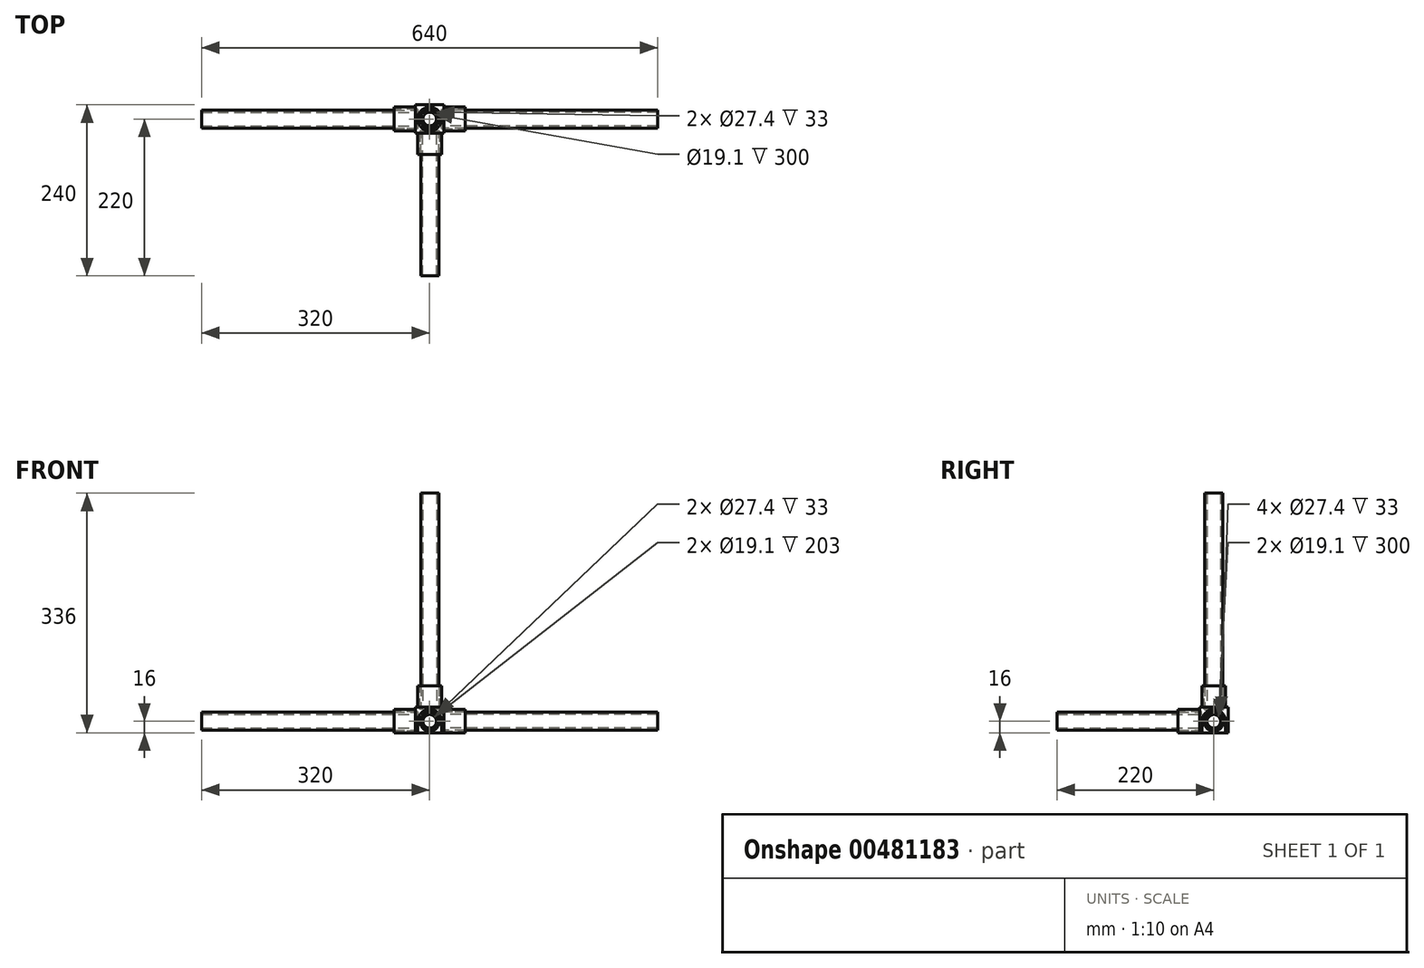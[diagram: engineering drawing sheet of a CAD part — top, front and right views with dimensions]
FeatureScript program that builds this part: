
annotation { "Feature Type Name" : "Feature", "Feature Type Description" : "" }
export const myFeature = defineFeature(function(context is Context, id is Id, definition is map)
    precondition{}
    {
        {
            var Q0;
            Q0=qCreatedBy(makeId("Front.planeOp"),FACE);
            var sketch = newSketch(context, id + "F0", { "sketchPlane" : qUnion([Q0])});
            skLineSegment(sketch, "E0.bottom", {"start": v(20, 20) * mm, "end": v(-20, 20) * mm});
            skLineSegment(sketch, "E0.top", {"start": v(20, -20) * mm, "end": v(-20, -20) * mm});
            skLineSegment(sketch, "E0.left", {"start": v(20, 20) * mm, "end": v(20, -20) * mm});
            skLineSegment(sketch, "E0.right", {"start": v(-20, 20) * mm, "end": v(-20, -20) * mm});
            skPoint(sketch, "E0.middle", {"position": v(0, 0) * mm});
            skSolve(sketch);
        }
        {
            var Q0;
            Q0=makeQuery(id+"F0.imprint","IMPRINT",FACE,{"disambiguationData":[TD([[makeQuery(id+"F0.imprint","IMPRINT",EDGE,{"derivedFrom":sQuery(id+"F0.wireOp",EDGE,"E0.bottom")}),1.0]])]});
            extrude(context, id + "F1", {"entities" : qUnion([Q0]), "endBound" : BoundingType.SYMMETRIC, "depth" : 40 * mm});
        }
        {
            var Q0;
            Q0=makeQuery(id+"F1.opExtrude","CAP_FACE",FACE,{"disambiguationData":[OSD([sQuery(id+"F0.wireOp",EDGE,"E0.bottom"),sQuery(id+"F0.wireOp",EDGE,"E0.top"),sQuery(id+"F0.wireOp",EDGE,"E0.left"),sQuery(id+"F0.wireOp",EDGE,"E0.right")])],"isStart":false});
            var sketch = newSketch(context, id + "F2", { "sketchPlane" : qUnion([Q0])});
            skLineSegment(sketch, "E1.bottom", {"start": v(20, 20) * mm, "end": v(-20, 20) * mm});
            skLineSegment(sketch, "E1.top", {"start": v(20, -20) * mm, "end": v(-20, -20) * mm});
            skLineSegment(sketch, "E1.left", {"start": v(20, 20) * mm, "end": v(20, -20) * mm});
            skLineSegment(sketch, "E1.right", {"start": v(-20, 20) * mm, "end": v(-20, -20) * mm});
            skPoint(sketch, "E1.middle", {"position": v(0, 0) * mm});
            skCircle(sketch, "E2", {"center": v(0, 0) * mm, "radius": 12.7 * mm});
            skCircle(sketch, "E3.0", {"center": v(0, 0) * mm, "radius": 9.55 * mm});
            skCircle(sketch, "E4.0", {"center": v(0, 0) * mm, "radius": 13.7 * mm});
            skCircle(sketch, "E5.0", {"center": v(0, 0) * mm, "radius": 16.7 * mm});
            skSolve(sketch);
        }
        {
            var Q0;
            Q0=makeQuery(id+"F2.imprint","IMPRINT",FACE,{"disambiguationData":[TD([[makeQuery(id+"F2.imprint","IMPRINT",EDGE,{"derivedFrom":sQuery(id+"F2.wireOp",EDGE,"E2")}),-1.0]])]});
            var Q1;
            Q1=makeQuery(id+"F2.imprint","IMPRINT",FACE,{"disambiguationData":[TD([[makeQuery(id+"F2.imprint","IMPRINT",EDGE,{"derivedFrom":sQuery(id+"F2.wireOp",EDGE,"E2")}),1.0]])]});
            var Q2;
            Q2=makeQuery(id+"F2.imprint","IMPRINT",FACE,{"disambiguationData":[TD([[makeQuery(id+"F2.imprint","IMPRINT",EDGE,{"derivedFrom":sQuery(id+"F2.wireOp",EDGE,"E3.0")}),1.0]])]});
            extrude(context, id + "F3", {"entities" : qUnion([Q0, Q1, Q2]), "operationType" : NewBodyOperationType.REMOVE, "oppositeDirection" : true, "depth" : 3 * mm});
        }
        {
            var Q0;
            Q0=makeQuery(id+"F2.imprint","IMPRINT",FACE,{"disambiguationData":[TD([[makeQuery(id+"F2.imprint","IMPRINT",EDGE,{"derivedFrom":sQuery(id+"F2.wireOp",EDGE,"E2")}),1.0]])]});
            extrude(context, id + "F4", {"entities" : qUnion([Q0]), "depth" : 200 * mm});
        }
        {
            var Q0;
            Q0=makeQuery(id+"F4.opExtrude","CAP_FACE",FACE,{"disambiguationData":[OSD([sQuery(id+"F2.wireOp",EDGE,"E2"),sQuery(id+"F2.wireOp",EDGE,"E3.0")])],"isStart":true});
            extrude(context, id + "F5", {"entities" : qUnion([Q0]), "operationType" : NewBodyOperationType.ADD, "depth" : 3 * mm});
        }
        {
            var Q0;
            Q0=makeQuery(id+"F2.imprint","IMPRINT",FACE,{"disambiguationData":[TD([[makeQuery(id+"F2.imprint","IMPRINT",EDGE,{"derivedFrom":sQuery(id+"F2.wireOp",EDGE,"E4.0")}),-1.0]])]});
            extrude(context, id + "F6", {"entities" : qUnion([Q0]), "operationType" : NewBodyOperationType.ADD, "depth" : 30 * mm});
        }
        {
            var Q0;
            Q0=makeQuery(id+"F1.opExtrude","SWEPT_FACE",FACE,{"disambiguationData":[OSD([sQuery(id+"F0.wireOp",EDGE,"E0.left")])]});
            var sketch = newSketch(context, id + "F7", { "sketchPlane" : qUnion([Q0])});
            skLineSegment(sketch, "E6.bottom", {"start": v(20, 20) * mm, "end": v(-20, 20) * mm});
            skLineSegment(sketch, "E6.top", {"start": v(20, -20) * mm, "end": v(-20, -20) * mm});
            skLineSegment(sketch, "E6.left", {"start": v(20, 20) * mm, "end": v(20, -20) * mm});
            skLineSegment(sketch, "E6.right", {"start": v(-20, 20) * mm, "end": v(-20, -20) * mm});
            skPoint(sketch, "E6.middle", {"position": v(0, 0) * mm});
            skCircle(sketch, "E7", {"center": v(0, 0) * mm, "radius": 12.7 * mm});
            skCircle(sketch, "E8.0", {"center": v(0, 0) * mm, "radius": 9.55 * mm});
            skCircle(sketch, "E9.0", {"center": v(0, 0) * mm, "radius": 13.7 * mm});
            skCircle(sketch, "E10.0", {"center": v(0, 0) * mm, "radius": 16.7 * mm});
            skSolve(sketch);
        }
        {
            var Q0;
            Q0=makeQuery(id+"F7.imprint","IMPRINT",FACE,{"disambiguationData":[TD([[makeQuery(id+"F7.imprint","IMPRINT",EDGE,{"derivedFrom":sQuery(id+"F7.wireOp",EDGE,"E7")}),-1.0]])]});
            var Q1;
            Q1=makeQuery(id+"F7.imprint","IMPRINT",FACE,{"disambiguationData":[TD([[makeQuery(id+"F7.imprint","IMPRINT",EDGE,{"derivedFrom":sQuery(id+"F7.wireOp",EDGE,"E7")}),1.0]])]});
            var Q2;
            Q2=makeQuery(id+"F7.imprint","IMPRINT",FACE,{"disambiguationData":[TD([[makeQuery(id+"F7.imprint","IMPRINT",EDGE,{"derivedFrom":sQuery(id+"F7.wireOp",EDGE,"E8.0")}),1.0]])]});
            extrude(context, id + "F8", {"entities" : qUnion([Q0, Q1, Q2]), "operationType" : NewBodyOperationType.REMOVE, "oppositeDirection" : true, "depth" : 3 * mm});
        }
        {
            var Q0;
            Q0=makeQuery(id+"F7.imprint","IMPRINT",FACE,{"disambiguationData":[TD([[makeQuery(id+"F7.imprint","IMPRINT",EDGE,{"derivedFrom":sQuery(id+"F7.wireOp",EDGE,"E7")}),1.0]])]});
            extrude(context, id + "F9", {"entities" : qUnion([Q0]), "depth" : 300 * mm});
        }
        {
            var Q0;
            Q0=makeQuery(id+"F7.imprint","IMPRINT",FACE,{"disambiguationData":[TD([[makeQuery(id+"F7.imprint","IMPRINT",EDGE,{"derivedFrom":sQuery(id+"F7.wireOp",EDGE,"E9.0")}),-1.0]])]});
            extrude(context, id + "F10", {"entities" : qUnion([Q0]), "operationType" : NewBodyOperationType.ADD, "depth" : 30 * mm});
        }
        {
            var Q0;
            Q0=makeQuery(id+"F1.opExtrude","SWEPT_FACE",FACE,{"disambiguationData":[OSD([sQuery(id+"F0.wireOp",EDGE,"E0.right")])]});
            var sketch = newSketch(context, id + "F11", { "sketchPlane" : qUnion([Q0])});
            skLineSegment(sketch, "E11.bottom", {"start": v(20, 20) * mm, "end": v(-20, 20) * mm});
            skLineSegment(sketch, "E11.top", {"start": v(20, -20) * mm, "end": v(-20, -20) * mm});
            skLineSegment(sketch, "E11.left", {"start": v(20, 20) * mm, "end": v(20, -20) * mm});
            skLineSegment(sketch, "E11.right", {"start": v(-20, 20) * mm, "end": v(-20, -20) * mm});
            skPoint(sketch, "E11.middle", {"position": v(0, 0) * mm});
            skCircle(sketch, "E12", {"center": v(0, 0) * mm, "radius": 12.7 * mm});
            skCircle(sketch, "E13.0", {"center": v(0, 0) * mm, "radius": 9.55 * mm});
            skCircle(sketch, "E14.0", {"center": v(0, 0) * mm, "radius": 13.7 * mm});
            skCircle(sketch, "E15.0", {"center": v(0, 0) * mm, "radius": 16.7 * mm});
            skSolve(sketch);
        }
        {
            var Q0;
            Q0=makeQuery(id+"F11.imprint","IMPRINT",FACE,{"disambiguationData":[TD([[makeQuery(id+"F11.imprint","IMPRINT",EDGE,{"derivedFrom":sQuery(id+"F11.wireOp",EDGE,"E12")}),-1.0]])]});
            var Q1;
            Q1=makeQuery(id+"F11.imprint","IMPRINT",FACE,{"disambiguationData":[TD([[makeQuery(id+"F11.imprint","IMPRINT",EDGE,{"derivedFrom":sQuery(id+"F11.wireOp",EDGE,"E12")}),1.0]])]});
            var Q2;
            Q2=makeQuery(id+"F11.imprint","IMPRINT",FACE,{"disambiguationData":[TD([[makeQuery(id+"F11.imprint","IMPRINT",EDGE,{"derivedFrom":sQuery(id+"F11.wireOp",EDGE,"E13.0")}),1.0]])]});
            extrude(context, id + "F12", {"entities" : qUnion([Q0, Q1, Q2]), "operationType" : NewBodyOperationType.REMOVE, "oppositeDirection" : true, "depth" : 3 * mm});
        }
        {
            var Q0;
            Q0=makeQuery(id+"F11.imprint","IMPRINT",FACE,{"disambiguationData":[TD([[makeQuery(id+"F11.imprint","IMPRINT",EDGE,{"derivedFrom":sQuery(id+"F11.wireOp",EDGE,"E12")}),1.0]])]});
            extrude(context, id + "F13", {"entities" : qUnion([Q0]), "depth" : 300 * mm});
        }
        {
            var Q0;
            Q0=makeQuery(id+"F11.imprint","IMPRINT",FACE,{"disambiguationData":[TD([[makeQuery(id+"F11.imprint","IMPRINT",EDGE,{"derivedFrom":sQuery(id+"F11.wireOp",EDGE,"E14.0")}),-1.0]])]});
            extrude(context, id + "F14", {"entities" : qUnion([Q0]), "operationType" : NewBodyOperationType.ADD, "depth" : 30 * mm});
        }
        {
            var Q0;
            Q0=makeQuery(id+"F1.opExtrude","SWEPT_FACE",FACE,{"disambiguationData":[OSD([sQuery(id+"F0.wireOp",EDGE,"E0.bottom")])]});
            var sketch = newSketch(context, id + "F15", { "sketchPlane" : qUnion([Q0])});
            skLineSegment(sketch, "E16.bottom", {"start": v(20, 20) * mm, "end": v(-20, 20) * mm});
            skLineSegment(sketch, "E16.top", {"start": v(20, -20) * mm, "end": v(-20, -20) * mm});
            skLineSegment(sketch, "E16.left", {"start": v(20, 20) * mm, "end": v(20, -20) * mm});
            skLineSegment(sketch, "E16.right", {"start": v(-20, 20) * mm, "end": v(-20, -20) * mm});
            skPoint(sketch, "E16.middle", {"position": v(0, 0) * mm});
            skCircle(sketch, "E17", {"center": v(0, 0) * mm, "radius": 12.7 * mm});
            skCircle(sketch, "E18.0", {"center": v(0, 0) * mm, "radius": 9.55 * mm});
            skCircle(sketch, "E19.0", {"center": v(0, 0) * mm, "radius": 13.7 * mm});
            skCircle(sketch, "E20.0", {"center": v(0, 0) * mm, "radius": 16.7 * mm});
            skSolve(sketch);
        }
        {
            var Q0;
            Q0=makeQuery(id+"F15.imprint","IMPRINT",FACE,{"disambiguationData":[TD([[makeQuery(id+"F15.imprint","IMPRINT",EDGE,{"derivedFrom":sQuery(id+"F15.wireOp",EDGE,"E17")}),-1.0]])]});
            var Q1;
            Q1=makeQuery(id+"F15.imprint","IMPRINT",FACE,{"disambiguationData":[TD([[makeQuery(id+"F15.imprint","IMPRINT",EDGE,{"derivedFrom":sQuery(id+"F15.wireOp",EDGE,"E17")}),1.0]])]});
            var Q2;
            Q2=makeQuery(id+"F15.imprint","IMPRINT",FACE,{"disambiguationData":[TD([[makeQuery(id+"F15.imprint","IMPRINT",EDGE,{"derivedFrom":sQuery(id+"F15.wireOp",EDGE,"E18.0")}),1.0]])]});
            extrude(context, id + "F16", {"entities" : qUnion([Q0, Q1, Q2]), "operationType" : NewBodyOperationType.REMOVE, "oppositeDirection" : true, "depth" : 3 * mm});
        }
        {
            var Q0;
            Q0=makeQuery(id+"F15.imprint","IMPRINT",FACE,{"disambiguationData":[TD([[makeQuery(id+"F15.imprint","IMPRINT",EDGE,{"derivedFrom":sQuery(id+"F15.wireOp",EDGE,"E17")}),1.0]])]});
            extrude(context, id + "F17", {"entities" : qUnion([Q0]), "depth" : 300 * mm});
        }
        {
            var Q0;
            Q0=makeQuery(id+"F15.imprint","IMPRINT",FACE,{"disambiguationData":[TD([[makeQuery(id+"F15.imprint","IMPRINT",EDGE,{"derivedFrom":sQuery(id+"F15.wireOp",EDGE,"E19.0")}),-1.0]])]});
            extrude(context, id + "F18", {"entities" : qUnion([Q0]), "operationType" : NewBodyOperationType.ADD, "depth" : 30 * mm});
        }
        {
            var Q0;
            Q0=makeQuery(id+"F1.opExtrude","SWEPT_FACE",FACE,{"disambiguationData":[OSD([sQuery(id+"F0.wireOp",EDGE,"E0.right")])]});
            var sketch = newSketch(context, id + "F19", { "sketchPlane" : qUnion([Q0])});
            skLineSegment(sketch, "E21", {"start": v(-16.7, 0) * mm, "end": v(-16.7, -20) * mm});
            skLineSegment(sketch, "E22", {"start": v(16.7, 0) * mm, "end": v(16.7, -20) * mm});
            skLineSegment(sketch, "E23", {"start": v(16.7, -20) * mm, "end": v(-16.7, -20) * mm});
            skSolve(sketch);
        }
        {
            var Q0;
            Q0=makeQuery(id+"F1.opExtrude","CAP_FACE",FACE,{"disambiguationData":[OSD([sQuery(id+"F0.wireOp",EDGE,"E0.bottom"),sQuery(id+"F0.wireOp",EDGE,"E0.top"),sQuery(id+"F0.wireOp",EDGE,"E0.left"),sQuery(id+"F0.wireOp",EDGE,"E0.right")])],"isStart":false});
            var sketch = newSketch(context, id + "F20", { "sketchPlane" : qUnion([Q0])});
            skLineSegment(sketch, "E24", {"start": v(-16.7, 0) * mm, "end": v(-16.7, -20) * mm});
            skPoint(sketch, "E24.startSnap0", {"position": v(-20, 0) * mm});
            skLineSegment(sketch, "E25", {"start": v(16.7, 0) * mm, "end": v(16.7, -20) * mm});
            skLineSegment(sketch, "E26", {"start": v(16.7, -20) * mm, "end": v(-16.7, -20) * mm});
            skSolve(sketch);
        }
        {
            var Q0;
            {var subQ0=sQuery(id+"F19.wireOp",EDGE,"E21");Q0=makeQuery(id+"F19.imprint","IMPRINT",FACE,{"disambiguationData":[TD([[makeQuery(id+"F19.imprint","IMPRINT",EDGE,{"derivedFrom":subQ0}),1.0]])]});}
            var Q1;
            Q1=makeQuery(id+"F14.opExtrude","CAP_FACE",FACE,{"disambiguationData":[OSD([sQuery(id+"F11.wireOp",EDGE,"E14.0"),sQuery(id+"F11.wireOp",EDGE,"E15.0")])],"isStart":false});
            extrude(context, id + "F21", {"entities" : qUnion([Q0]), "operationType" : NewBodyOperationType.ADD, "endBound" : BoundingType.UP_TO_SURFACE, "endBoundEntityFace" : qUnion([Q1]), "depth" : 25 * mm});
        }
        {
            var Q0;
            {var subQ0=sQuery(id+"F20.wireOp",EDGE,"E24");Q0=makeQuery(id+"F20.imprint","IMPRINT",FACE,{"disambiguationData":[TD([[makeQuery(id+"F20.imprint","IMPRINT",EDGE,{"derivedFrom":subQ0}),1.0]])]});}
            var Q1;
            Q1=makeQuery(id+"F6.opExtrude","CAP_FACE",FACE,{"disambiguationData":[OSD([sQuery(id+"F2.wireOp",EDGE,"E4.0"),sQuery(id+"F2.wireOp",EDGE,"E5.0")])],"isStart":false});
            extrude(context, id + "F22", {"entities" : qUnion([Q0]), "operationType" : NewBodyOperationType.ADD, "endBound" : BoundingType.UP_TO_SURFACE, "endBoundEntityFace" : qUnion([Q1]), "depth" : 25 * mm});
        }
        {
            var Q0;
            Q0=makeQuery(id+"F1.opExtrude","SWEPT_FACE",FACE,{"disambiguationData":[OSD([sQuery(id+"F0.wireOp",EDGE,"E0.left")])]});
            var sketch = newSketch(context, id + "F23", { "sketchPlane" : qUnion([Q0])});
            skLineSegment(sketch, "E27", {"start": v(-16.7, 0) * mm, "end": v(-16.7, -20) * mm});
            skLineSegment(sketch, "E28", {"start": v(16.7, 0) * mm, "end": v(16.7, -20) * mm});
            skLineSegment(sketch, "E29", {"start": v(16.7, -20) * mm, "end": v(-16.7, -20) * mm});
            skSolve(sketch);
        }
        {
            var Q0;
            {var subQ0=sQuery(id+"F23.wireOp",EDGE,"E27");Q0=makeQuery(id+"F23.imprint","IMPRINT",FACE,{"disambiguationData":[TD([[makeQuery(id+"F23.imprint","IMPRINT",EDGE,{"derivedFrom":subQ0}),1.0]])]});}
            var Q1;
            Q1=makeQuery(id+"F10.opExtrude","CAP_FACE",FACE,{"disambiguationData":[OSD([sQuery(id+"F7.wireOp",EDGE,"E9.0"),sQuery(id+"F7.wireOp",EDGE,"E10.0")])],"isStart":false});
            extrude(context, id + "F24", {"entities" : qUnion([Q0]), "operationType" : NewBodyOperationType.ADD, "endBound" : BoundingType.UP_TO_SURFACE, "endBoundEntityFace" : qUnion([Q1]), "depth" : 25 * mm});
        }
        {
            var Q0;
            Q0=makeQuery(id+"F24.boolean.opBoolean","MERGE",FACE,{"derivedFrom":[makeQuery(id+"F22.boolean.opBoolean","MERGE",FACE,{"derivedFrom":[makeQuery(id+"F21.boolean.opBoolean","MERGE",FACE,{"derivedFrom":[makeQuery(id+"F1.opExtrude","SWEPT_FACE",FACE,{"disambiguationData":[OSD([sQuery(id+"F0.wireOp",EDGE,"E0.top")])]}),makeQuery(id+"F21.opExtrude","SWEPT_FACE",FACE,{"disambiguationData":[OSD([sQuery(id+"F19.wireOp",EDGE,"E23")])]})]}),makeQuery(id+"F22.opExtrude","SWEPT_FACE",FACE,{"disambiguationData":[OSD([sQuery(id+"F20.wireOp",EDGE,"E26")])]})]}),makeQuery(id+"F24.opExtrude","SWEPT_FACE",FACE,{"disambiguationData":[OSD([sQuery(id+"F23.wireOp",EDGE,"E29")])]})]});
            extrude(context, id + "F25", {"entities" : qUnion([Q0]), "operationType" : NewBodyOperationType.REMOVE, "oppositeDirection" : true, "depth" : 4 * mm});
        }
        {
            var Q0;
            Q0=makeQuery(id+"F1.opExtrude","SWEPT_BODY",BODY,{"disambiguationData":[OSD([sQuery(id+"F0.wireOp",EDGE,"E0.bottom"),sQuery(id+"F0.wireOp",EDGE,"E0.top"),sQuery(id+"F0.wireOp",EDGE,"E0.left"),sQuery(id+"F0.wireOp",EDGE,"E0.right")])]});
            transform(context, id + "F26", {"entities" : qUnion([Q0]), "transformType" : TransformType.TRANSLATION_3D, "dx" : 0 * mm, "dy" : 0 * mm, "dz" : 0 * mm, "makeCopy" : true});
        }
    });
